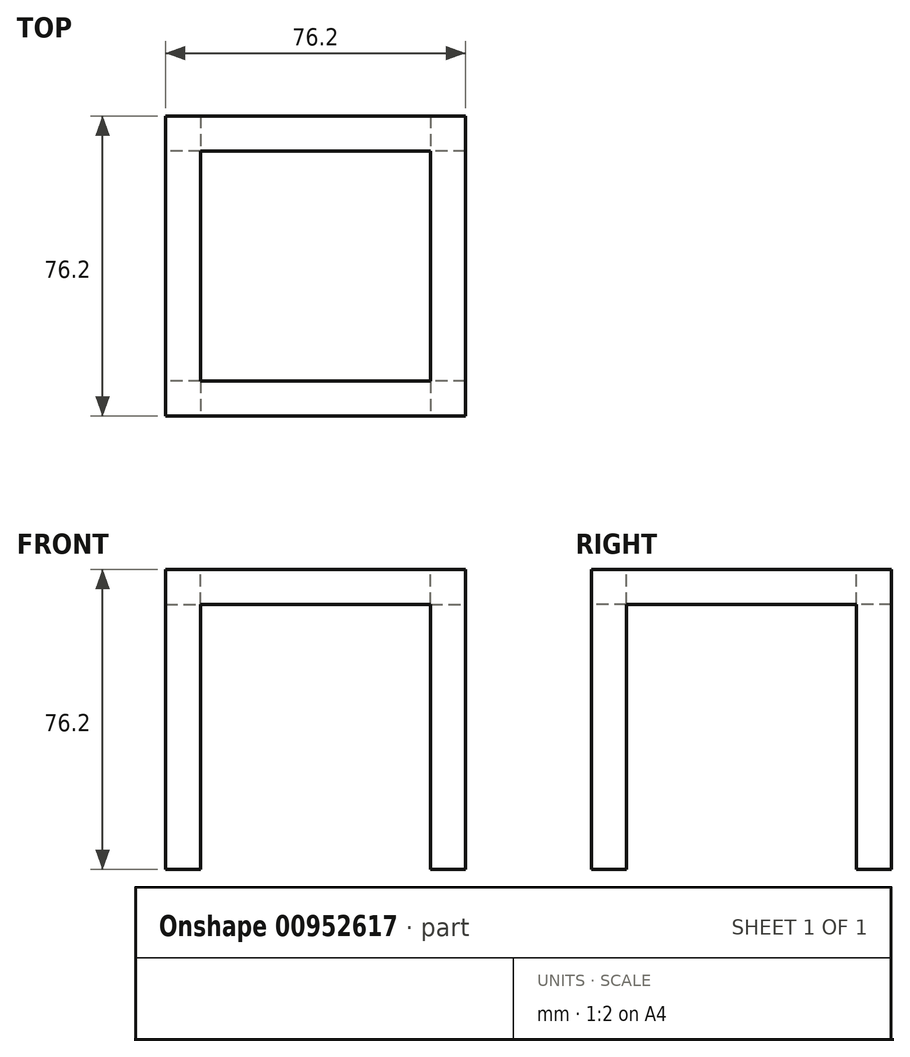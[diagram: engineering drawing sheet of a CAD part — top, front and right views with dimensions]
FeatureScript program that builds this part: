
annotation { "Feature Type Name" : "Feature", "Feature Type Description" : "" }
export const myFeature = defineFeature(function(context is Context, id is Id, definition is map)
    precondition{}
    {
        {
            var Q0;
            Q0=qCreatedBy(makeId("Top.planeOp"),FACE);
            var sketch = newSketch(context, id + "F0", { "sketchPlane" : qUnion([Q0])});
            skLineSegment(sketch, "E0.bottom", {"start": v(0, 0) * mm, "end": v(76.2, 0) * mm});
            skLineSegment(sketch, "E0.top", {"start": v(0, -76.2) * mm, "end": v(76.2, -76.2) * mm});
            skLineSegment(sketch, "E0.left", {"start": v(0, 0) * mm, "end": v(0, -76.2) * mm});
            skLineSegment(sketch, "E0.right", {"start": v(76.2, 0) * mm, "end": v(76.2, -76.2) * mm});
            skSolve(sketch);
        }
        {
            var Q0;
            Q0=makeQuery(id+"F0.imprint","IMPRINT",FACE,{"disambiguationData":[TD([[makeQuery(id+"F0.imprint","IMPRINT",EDGE,{"derivedFrom":sQuery(id+"F0.wireOp",EDGE,"E0.bottom")}),-1.0]])]});
            extrude(context, id + "F1", {"entities" : qUnion([Q0]), "depth" : 76.2 * mm, "offsetDistance" : 25.4 * mm});
        }
        {
            var Q0;
            Q0=makeQuery(id+"F1.opExtrude","CAP_FACE",FACE,{"disambiguationData":[OSD([sQuery(id+"F0.wireOp",EDGE,"E0.bottom"),sQuery(id+"F0.wireOp",EDGE,"E0.top"),sQuery(id+"F0.wireOp",EDGE,"E0.left"),sQuery(id+"F0.wireOp",EDGE,"E0.right")])],"isStart":false});
            var sketch = newSketch(context, id + "F2", { "sketchPlane" : qUnion([Q0])});
            skLineSegment(sketch, "E1.bottom", {"start": v(67.31, -67.31) * mm, "end": v(8.9, -67.31) * mm});
            skLineSegment(sketch, "E1.top", {"start": v(67.31, -8.9) * mm, "end": v(8.9, -8.9) * mm});
            skLineSegment(sketch, "E1.left", {"start": v(67.31, -67.31) * mm, "end": v(67.31, -8.9) * mm});
            skLineSegment(sketch, "E1.right", {"start": v(8.9, -67.31) * mm, "end": v(8.9, -8.9) * mm});
            skPoint(sketch, "E1.middle", {"position": v(38.1, -38.1) * mm});
            skPoint(sketch, "E2.trimOffspring.end.orphan", {"position": v(0, -76.2) * mm});
            skPoint(sketch, "E3.start.orphan", {"position": v(76.2, 0) * mm});
            skSolve(sketch);
        }
        {
            var Q0;
            Q0=makeQuery(id+"F2.imprint","IMPRINT",FACE,{"disambiguationData":[TD([[makeQuery(id+"F2.imprint","IMPRINT",EDGE,{"derivedFrom":sQuery(id+"F2.wireOp",EDGE,"E1.bottom")}),-1.0]])]});
            extrude(context, id + "F3", {"entities" : qUnion([Q0]), "operationType" : NewBodyOperationType.REMOVE, "oppositeDirection" : true, "depth" : 76.2 * mm, "offsetDistance" : 25.4 * mm});
        }
        {
            var Q0;
            Q0=makeQuery(id+"F1.opExtrude","SWEPT_FACE",FACE,{"disambiguationData":[OSD([sQuery(id+"F0.wireOp",EDGE,"E0.right")])]});
            var sketch = newSketch(context, id + "F4", { "sketchPlane" : qUnion([Q0])});
            skLineSegment(sketch, "E4.bottom", {"start": v(-8.9, 67.31) * mm, "end": v(-67.31, 67.31) * mm});
            skLineSegment(sketch, "E4.left", {"start": v(-8.9, 67.31) * mm, "end": v(-8.9, 0) * mm});
            skLineSegment(sketch, "E4.right", {"start": v(-67.31, 67.31) * mm, "end": v(-67.31, 0) * mm});
            skPoint(sketch, "E4.middle", {"position": v(-38.1, 0) * mm});
            skPoint(sketch, "E5", {"position": v(-67.31, 0) * mm});
            skPoint(sketch, "E6", {"position": v(-8.9, 0) * mm});
            skSolve(sketch);
        }
        {
            var Q0;
            Q0=makeQuery(id+"F4.imprint","IMPRINT",FACE,{"disambiguationData":[TD([[makeQuery(id+"F4.imprint","IMPRINT",EDGE,{"derivedFrom":sQuery(id+"F4.wireOp",EDGE,"E4.bottom")}),1.0]])]});
            extrude(context, id + "F5", {"entities" : qUnion([Q0]), "operationType" : NewBodyOperationType.REMOVE, "oppositeDirection" : true, "depth" : 76.2 * mm, "offsetDistance" : 25.4 * mm});
        }
        {
            var Q0;
            Q0=makeQuery(id+"F1.opExtrude","SWEPT_FACE",FACE,{"disambiguationData":[OSD([sQuery(id+"F0.wireOp",EDGE,"E0.top")])]});
            var sketch = newSketch(context, id + "F6", { "sketchPlane" : qUnion([Q0])});
            skLineSegment(sketch, "E7.bottom", {"start": v(67.31, 67.31) * mm, "end": v(8.89, 67.31) * mm});
            skLineSegment(sketch, "E7.top", {"start": v(67.31, -67.31) * mm, "end": v(8.9, -67.31) * mm});
            skLineSegment(sketch, "E7.left", {"start": v(67.31, 67.31) * mm, "end": v(67.31, -67.31) * mm});
            skLineSegment(sketch, "E7.right", {"start": v(8.89, 67.31) * mm, "end": v(8.9, -67.31) * mm});
            skPoint(sketch, "E7.middle", {"position": v(38.1, 0) * mm});
            skSolve(sketch);
        }
        {
            var Q0;
            Q0 = qSketchRegion(id + "F6", true);
            extrude(context, id + "F7", {"entities" : qUnion([Q0]), "operationType" : NewBodyOperationType.REMOVE, "oppositeDirection" : true, "depth" : 76.2 * mm, "offsetDistance" : 25.4 * mm});
        }
    });
